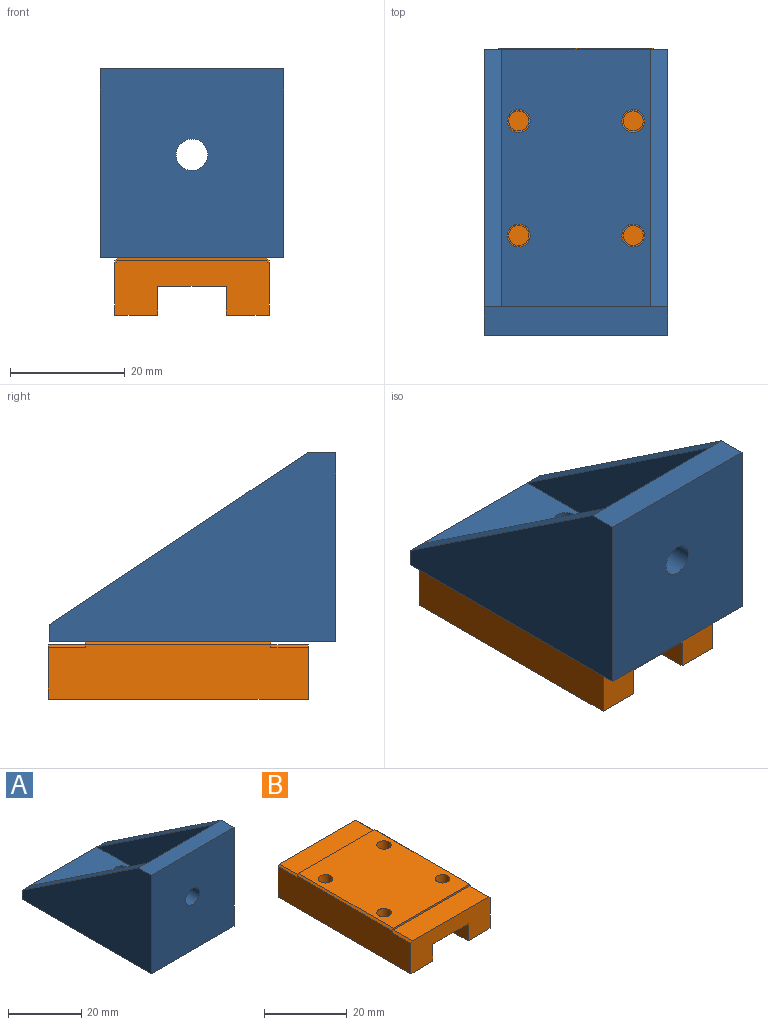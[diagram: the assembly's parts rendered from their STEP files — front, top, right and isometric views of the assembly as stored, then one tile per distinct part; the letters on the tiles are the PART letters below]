
ASSEMBLY  parts=2 mates=1
PART A: 17 faces, bbox 32x50x33 mm
  f0: plane 45x26mm, normal (0,0,1), area 1119.7mm2, adj f1,f2,f3,f4,f5,f6,f12,f14
  f1: plane 30x26mm, normal (0,1,0), area 756.2mm2, adj f0,f8,f9,f12,f14
  f2: plane 32x3mm, normal (0,1,0), area 96mm2, adj f0,f7,f11,f13,f15,f16
  f3: cylinder r=2mm len=4mm, axis (0,0,-1), area 37.7mm2, adj f0,f7
  f4: cylinder r=2mm len=4mm, axis (0,0,-1), area 37.7mm2, adj f0,f7
  f5: cylinder r=2mm len=4mm, axis (0,0,-1), area 37.7mm2, adj f0,f7
  f6: cylinder r=2mm len=4mm, axis (0,0,-1), area 37.7mm2, adj f0,f7
  f7: plane 50x32mm, normal (0,0,-1), area 1549.7mm2, adj f2,f3,f4,f5,f6,f10,f15,f16
  f8: plane 32x5mm, normal (0,0,1), area 160mm2, adj f1,f10,f11,f13,f15,f16
  f9: cylinder r=2.75mm len=5.5mm, axis (0,1,0), area 86.4mm2, adj f1,f10
  f10: plane 33x32mm, normal (0,-1,0), area 1032.2mm2, adj f7,f8,f9,f15,f16
  f11: plane 45x30mm, normal (0,0.55,0.83), area 162.2mm2, adj f2,f8,f12,f16
  f12: plane 45x30mm, normal (-1,0,0), area 675mm2, adj f0,f1,f11
  f13: plane 45x30mm, normal (0,0.55,0.83), area 162.2mm2, adj f2,f8,f14,f15
  f14: plane 45x30mm, normal (1,0,0), area 675mm2, adj f0,f1,f13
  f15: plane 50x33mm, normal (-1,0,0), area 975mm2, adj f2,f7,f8,f10,f13
  f16: plane 50x33mm, normal (1,0,0), area 975mm2, adj f2,f7,f8,f10,f11
PART B: 28 faces, bbox 27x45.4x10 mm
  f0: plane 27x9.5mm, normal (0,-1,0), area 196.2mm2, adj f1,f3,f5,f6,f7,f8,f9,f19
  f1: plane 45.4x9.5mm, normal (1,0,0), area 424.8mm2, adj f0,f2,f5,f18,f20,f23,f25,f26
  f2: plane 27x9.5mm, normal (0,1,0), area 196.2mm2, adj f1,f3,f5,f6,f7,f8,f9,f21
  f3: plane 45.4x9.5mm, normal (-1,0,0), area 424.8mm2, adj f0,f2,f6,f18,f20,f22,f24,f27
  f4: plane 32.4x26mm, normal (0,0,1), area 803.9mm2, adj f10,f12,f14,f16,f18,f20,f22,f23
  f5: plane 45.4x7.5mm, normal (0,0,-1), area 340.5mm2, adj f0,f1,f2,f9
  f6: plane 45.4x7.5mm, normal (0,0,-1), area 340.5mm2, adj f0,f2,f3,f8
  f7: plane 45.4x12mm, normal (0,0,-1), area 544.8mm2, adj f0,f2,f8,f9
  f8: plane 45.4x5mm, normal (1,0,0), area 227mm2, adj f0,f2,f6,f7
  f9: plane 45.4x5mm, normal (-1,0,0), area 227mm2, adj f0,f2,f5,f7
  f10: cylinder r=1.75mm len=4.5mm, axis (0,0,1), area 49.5mm2, adj f4,f11
  f11: plane 3.5x3.5mm, normal (0,0,1), area 9.6mm2, adj f10
  f12: cylinder r=1.75mm len=4.5mm, axis (0,0,1), area 49.5mm2, adj f4,f13
  f13: plane 3.5x3.5mm, normal (0,0,1), area 9.6mm2, adj f12
  f14: cylinder r=1.75mm len=4.5mm, axis (0,0,1), area 49.5mm2, adj f4,f15
  f15: plane 3.5x3.5mm, normal (0,0,1), area 9.6mm2, adj f14
  f16: cylinder r=1.75mm len=4.5mm, axis (0,0,1), area 49.5mm2, adj f4,f17
  f17: plane 3.5x3.5mm, normal (0,0,1), area 9.6mm2, adj f16
  f18: plane 27x1mm, normal (0,-1,0), area 13.5mm2, adj f1,f3,f4,f19,f22,f23,f26,f27
  f19: plane 26x6.5mm, normal (0,0,1), area 169mm2, adj f0,f18,f26,f27
  f20: plane 27x1mm, normal (0,1,0), area 13.5mm2, adj f1,f3,f4,f21,f22,f23,f24,f25
  f21: plane 26x6.5mm, normal (0,0,1), area 169mm2, adj f2,f20,f24,f25
  f22: plane 32.4x0.5mm, normal (-0.71,0,0.71), area 22.9mm2, adj f3,f4,f18,f20
  f23: plane 32.4x0.5mm, normal (0.71,0,0.71), area 22.9mm2, adj f1,f4,f18,f20
  f24: plane 6.5x0.5mm, normal (-0.71,0,0.71), area 4.6mm2, adj f2,f3,f20,f21
  f25: plane 6.5x0.5mm, normal (0.71,0,0.71), area 4.6mm2, adj f1,f2,f20,f21
  f26: plane 6.5x0.5mm, normal (0.71,0,0.71), area 4.6mm2, adj f0,f1,f18,f19
  f27: plane 6.5x0.5mm, normal (-0.71,0,0.71), area 4.6mm2, adj f0,f3,f18,f19
PLACE A t=(-0.73,2.4,9.27)mm
PLACE B t=(-0.73,2.42,-0.73)mm
MATE fastened A.f7 <-> B.f4  axis (0,0,-1) through (-0.73,-0.18,9.27)mm
